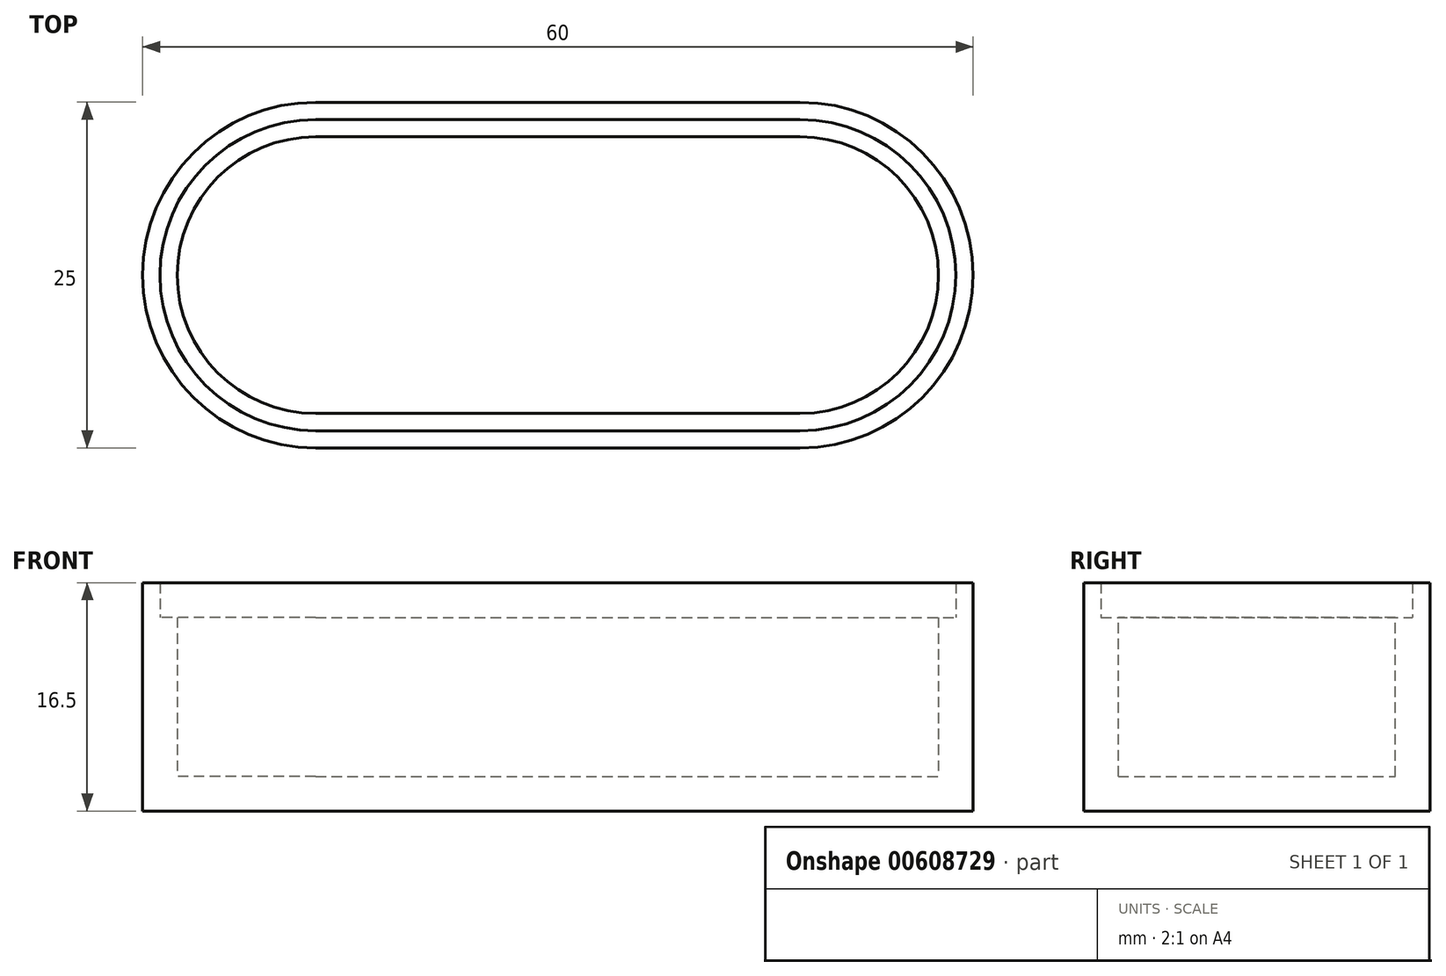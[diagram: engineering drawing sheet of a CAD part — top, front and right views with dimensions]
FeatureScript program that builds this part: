
annotation { "Feature Type Name" : "Feature", "Feature Type Description" : "" }
export const myFeature = defineFeature(function(context is Context, id is Id, definition is map)
    precondition{}
    {
        {
            var Q0;
            Q0=qCreatedBy(makeId("Top.planeOp"),FACE);
            var sketch = newSketch(context, id + "F0", { "sketchPlane" : qUnion([Q0])});
            skLineSegment(sketch, "E0.bottom", {"start": v(-9.66, -16.64) * mm, "end": v(25.34, -16.64) * mm});
            skLineSegment(sketch, "E0.top", {"start": v(-9.66, 8.36) * mm, "end": v(25.34, 8.36) * mm});
            skArc(sketch, "E1", {"start": v(25.34, -16.64) * mm, "mid": v(37.84, -4.14) * mm, "end": v(25.34, 8.36) * mm});
            skArc(sketch, "E2", {"start": v(-9.66, 8.36) * mm, "mid": v(-22.16, -4.14) * mm, "end": v(-9.66, -16.64) * mm});
            skSolve(sketch);
        }
        {
            var Q0;
            Q0=makeQuery(id+"F0.imprint","IMPRINT",FACE,{"disambiguationData":[TD([[makeQuery(id+"F0.imprint","IMPRINT",EDGE,{"derivedFrom":sQuery(id+"F0.wireOp",EDGE,"E0.bottom")}),1.0]])]});
            extrude(context, id + "F1", {"entities" : qUnion([Q0]), "depth" : 14 * mm, "offsetDistance" : 25 * mm});
        }
        {
            var Q0;
            Q0=makeQuery(id+"F1.opExtrude","CAP_FACE",FACE,{"disambiguationData":[OSD([sQuery(id+"F0.wireOp",EDGE,"E0.bottom"),sQuery(id+"F0.wireOp",EDGE,"E0.top"),sQuery(id+"F0.wireOp",EDGE,"E1"),sQuery(id+"F0.wireOp",EDGE,"E2")])],"isStart":false});
            shell(context, id + "F2", {"entities" : qUnion([Q0]), "thickness" : 2.5 * mm});
        }
        {
            var Q0;
            Q0=makeQuery(id+"F1.opExtrude","CAP_FACE",FACE,{"disambiguationData":[OSD([sQuery(id+"F0.wireOp",EDGE,"E0.bottom"),sQuery(id+"F0.wireOp",EDGE,"E0.top"),sQuery(id+"F0.wireOp",EDGE,"E1"),sQuery(id+"F0.wireOp",EDGE,"E2")])],"isStart":false});
            var sketch = newSketch(context, id + "F3", { "sketchPlane" : qUnion([Q0])});
            skLineSegment(sketch, "E3.0", {"start": v(25.34, 7.1) * mm, "end": v(-9.66, 7.1) * mm});
            skArc(sketch, "E3.1", {"start": v(25.34, -15.4) * mm, "mid": v(36.59, -4.14) * mm, "end": v(25.34, 7.1) * mm});
            skLineSegment(sketch, "E3.2", {"start": v(-9.66, -15.4) * mm, "end": v(25.34, -15.4) * mm});
            skArc(sketch, "E3.3", {"start": v(-9.66, 7.1) * mm, "mid": v(-20.91, -4.14) * mm, "end": v(-9.66, -15.4) * mm});
            skSolve(sketch);
        }
        {
            var Q0;
            Q0=makeQuery(id+"F3.imprint","IMPRINT",FACE,{"disambiguationData":[TD([[makeQuery(id+"F3.imprint","IMPRINT",EDGE,{"derivedFrom":sQuery(id+"F3.wireOp",EDGE,"E3.0")}),-1.0]])]});
            extrude(context, id + "F4", {"entities" : qUnion([Q0]), "operationType" : NewBodyOperationType.ADD, "depth" : 2.5 * mm, "offsetDistance" : 25 * mm});
        }
    });
